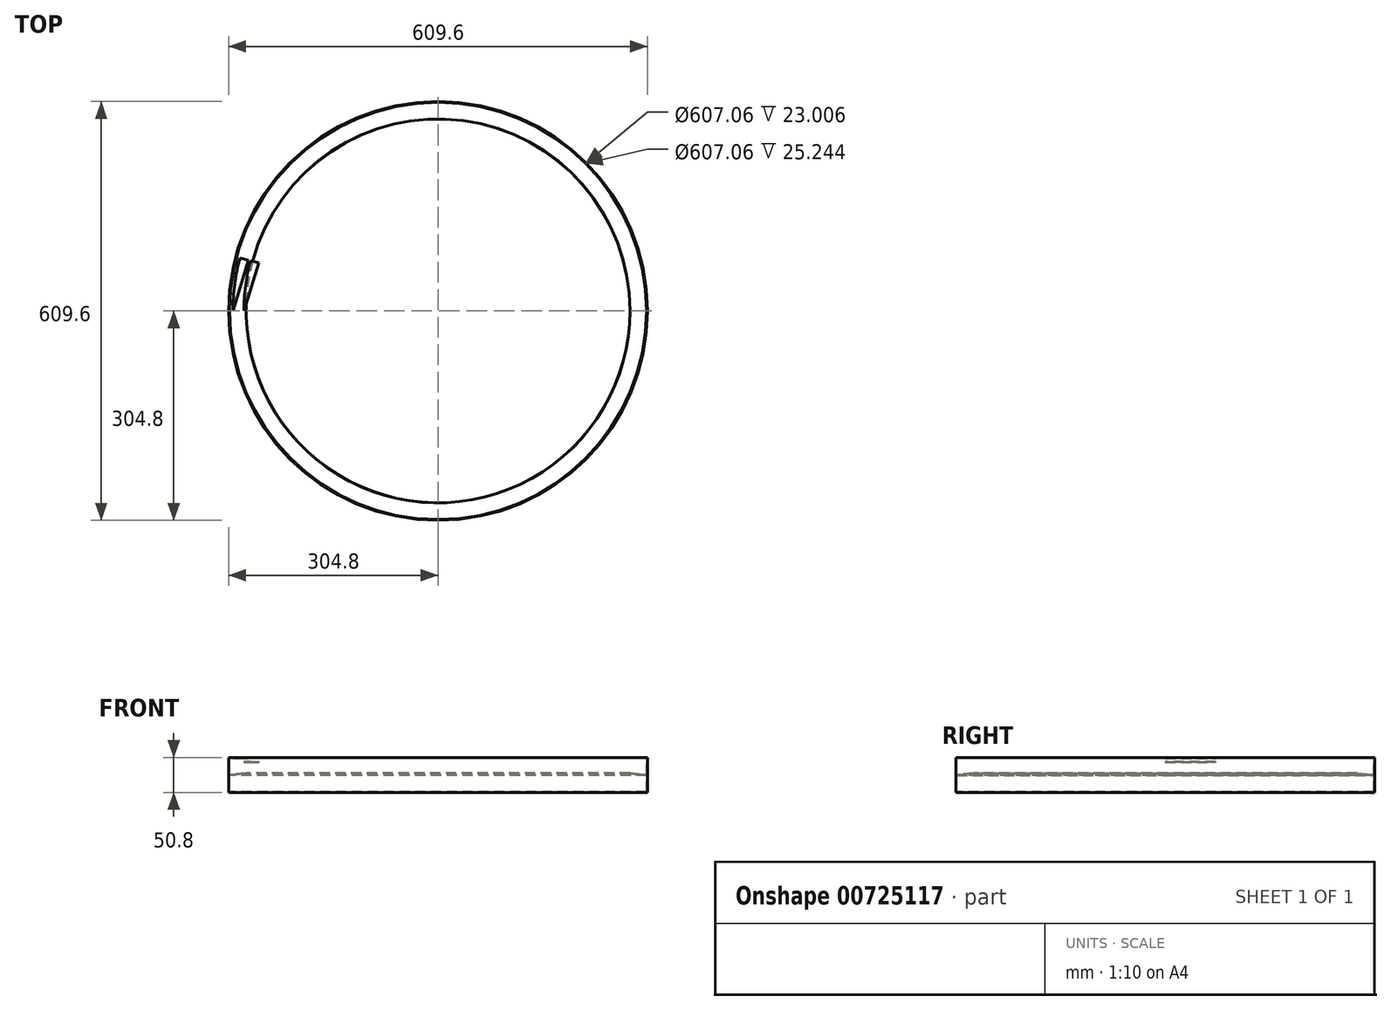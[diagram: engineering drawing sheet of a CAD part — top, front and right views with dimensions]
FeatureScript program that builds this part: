
annotation { "Feature Type Name" : "Feature", "Feature Type Description" : "" }
export const myFeature = defineFeature(function(context is Context, id is Id, definition is map)
    precondition{}
    {
        {
            var Q0;
            Q0=qCreatedBy(makeId("Front.planeOp"),FACE);
            var sketch = newSketch(context, id + "F0", { "sketchPlane" : qUnion([Q0])});
            skLineSegment(sketch, "E0.left", {"start": v(-304.8, -3.12) * mm, "end": v(-304.8, -28.52) * mm});
            skLineSegment(sketch, "E1", {"start": v(-279.4, 0) * mm, "end": v(-303.53, -2.96) * mm});
            skLineSegment(sketch, "E2", {"start": v(-279.4, 0) * mm, "end": v(-279.25, -1.26) * mm});
            skLineSegment(sketch, "E3", {"start": v(-279.25, -1.26) * mm, "end": v(-303.53, -4.24) * mm});
            skPoint(sketch, "E4.orphan", {"position": v(-304.8, 0) * mm});
            skLineSegment(sketch, "E5", {"start": v(-304.8, -3.12) * mm, "end": v(-304.8, 22.28) * mm});
            skLineSegment(sketch, "E6", {"start": v(-304.8, 22.28) * mm, "end": v(-303.53, 22.28) * mm});
            skLineSegment(sketch, "E7", {"start": v(-303.53, 22.28) * mm, "end": v(-303.53, -2.96) * mm});
            skLineSegment(sketch, "E8", {"start": v(-304.8, -28.52) * mm, "end": v(0, -28.52) * mm});
            skLineSegment(sketch, "E9", {"start": v(-303.53, -27.25) * mm, "end": v(-303.53, -4.24) * mm});
            skLineSegment(sketch, "E10", {"start": v(-303.53, -27.25) * mm, "end": v(0, -27.25) * mm});
            skLineSegment(sketch, "E11", {"start": v(0, -28.52) * mm, "end": v(0, -27.25) * mm});
            skSolve(sketch);
        }
        {
            var Q0;
            Q0=qCreatedBy(makeId("Front.planeOp"),FACE);
            var sketch = newSketch(context, id + "F1", { "sketchPlane" : qUnion([Q0])});
            skLineSegment(sketch, "E12", {"start": v(0, 40.5) * mm, "end": v(0, -62.38) * mm});
            skSolve(sketch);
        }
        {
            var Q0;
            Q0=makeQuery(id+"F0.imprint","IMPRINT",FACE,{"disambiguationData":[TD([[makeQuery(id+"F0.imprint","IMPRINT",EDGE,{"derivedFrom":sQuery(id+"F0.wireOp",EDGE,"E0.left")}),1.0]])]});
            var Q1;
            Q1=sQuery(id+"F1.wireOp",EDGE,"E12");
            revolve(context, id + "F2", {"surfaceOperationType" : NewSurfaceOperationType.NEW, "entities" : qUnion([Q0]), "axis" : qUnion([Q1]), "revolveType" : RevolveType.FULL});
        }
        {
            var Q0;
            Q0=qCreatedBy(makeId("Front.planeOp"),FACE);
            var sketch = newSketch(context, id + "F3", { "sketchPlane" : qUnion([Q0])});
            skLineSegment(sketch, "E13.bottom", {"start": v(-282.63, 16.5) * mm, "end": v(-269.93, 16.5) * mm});
            skLineSegment(sketch, "E13.top", {"start": v(-282.63, 15.24) * mm, "end": v(-269.93, 15.24) * mm});
            skLineSegment(sketch, "E13.left", {"start": v(-282.63, 16.5) * mm, "end": v(-282.63, 15.24) * mm});
            skLineSegment(sketch, "E13.right", {"start": v(-269.93, 16.5) * mm, "end": v(-269.93, 15.24) * mm});
            skLineSegment(sketch, "E14.bottom", {"start": v(-298.63, 22.22) * mm, "end": v(-285.93, 22.22) * mm});
            skLineSegment(sketch, "E14.top", {"start": v(-298.63, 20.95) * mm, "end": v(-285.93, 20.95) * mm});
            skLineSegment(sketch, "E14.left", {"start": v(-298.63, 22.22) * mm, "end": v(-298.63, 20.95) * mm});
            skLineSegment(sketch, "E14.right", {"start": v(-285.93, 22.22) * mm, "end": v(-285.93, 20.95) * mm});
            skSolve(sketch);
        }
        {
            var Q0;
            Q0 = qSketchRegion(id + "F3", true);
            var Q1;
            Q1=sQuery(id+"F1.wireOp",EDGE,"E12");
            revolve(context, id + "F4", {"surfaceOperationType" : NewSurfaceOperationType.NEW, "entities" : qUnion([Q0]), "axis" : qUnion([Q1]), "revolveType" : RevolveType.ONE_DIRECTION, "angle" : 15 * degree});
        }
        {
            var Q0;
            Q0=makeQuery(id+"F4.opRevolve","SWEPT_FACE",FACE,{"disambiguationData":[OSD([sQuery(id+"F3.wireOp",EDGE,"E14.bottom")])]});
            var sketch = newSketch(context, id + "F5", { "sketchPlane" : qUnion([Q0])});
            skLineSegment(sketch, "E15", {"start": v(-298.63, 0) * mm, "end": v(-276.19, 74) * mm});
            skLineSegment(sketch, "E16", {"start": v(-276.19, 74) * mm, "end": v(-285.93, 0) * mm});
            skLineSegment(sketch, "E17", {"start": v(-285.93, 0) * mm, "end": v(-298.63, 0) * mm});
            skSolve(sketch);
        }
        {
            var Q0;
            Q0=makeQuery(id+"F4.opRevolve","SWEPT_FACE",FACE,{"disambiguationData":[OSD([sQuery(id+"F3.wireOp",EDGE,"E13.bottom")])]});
            var sketch = newSketch(context, id + "F6", { "sketchPlane" : qUnion([Q0])});
            skLineSegment(sketch, "E18", {"start": v(-282.63, 0) * mm, "end": v(-260.73, 69.86) * mm});
            skLineSegment(sketch, "E19", {"start": v(-260.73, 69.86) * mm, "end": v(-269.93, 0) * mm});
            skLineSegment(sketch, "E20", {"start": v(-269.93, 0) * mm, "end": v(-282.63, 0) * mm});
            skSolve(sketch);
        }
        {
            var Q0;
            Q0 = qSketchRegion(id + "F5", true);
            extrude(context, id + "F7", {"entities" : qUnion([Q0]), "operationType" : NewBodyOperationType.REMOVE, "endBound" : BoundingType.UP_TO_NEXT, "oppositeDirection" : true, "depth" : 25.4 * mm, "offsetDistance" : 25.4 * mm});
        }
        {
            var Q0;
            Q0 = qSketchRegion(id + "F6", true);
            extrude(context, id + "F8", {"entities" : qUnion([Q0]), "operationType" : NewBodyOperationType.REMOVE, "endBound" : BoundingType.UP_TO_NEXT, "oppositeDirection" : true, "depth" : 25.4 * mm, "offsetDistance" : 25.4 * mm});
        }
    });
